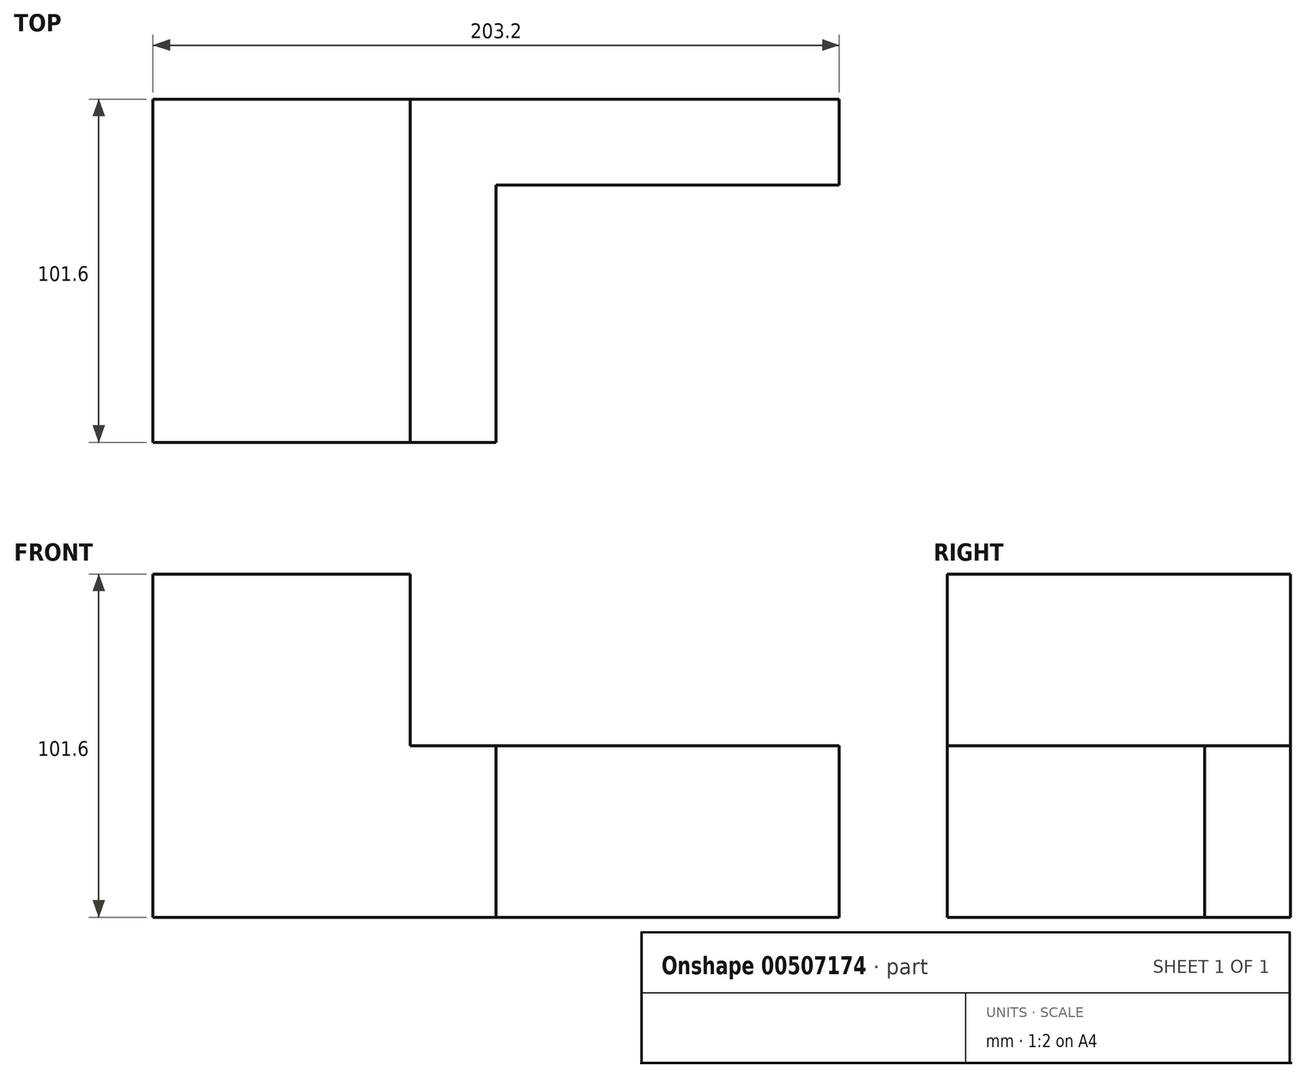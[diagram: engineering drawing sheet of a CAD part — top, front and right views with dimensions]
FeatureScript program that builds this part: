
annotation { "Feature Type Name" : "Feature", "Feature Type Description" : "" }
export const myFeature = defineFeature(function(context is Context, id is Id, definition is map)
    precondition{}
    {
        {
            var Q0;
            Q0=qCreatedBy(makeId("Front.planeOp"),FACE);
            var sketch = newSketch(context, id + "F0", { "sketchPlane" : qUnion([Q0])});
            skLineSegment(sketch, "E0", {"start": v(-76.2, 37.75) * mm, "end": v(0, 37.75) * mm});
            skLineSegment(sketch, "E1", {"start": v(0, 37.75) * mm, "end": v(0, -13.05) * mm});
            skLineSegment(sketch, "E2", {"start": v(0, -13.05) * mm, "end": v(127, -13.05) * mm});
            skLineSegment(sketch, "E3", {"start": v(127, -13.05) * mm, "end": v(127, -63.85) * mm});
            skLineSegment(sketch, "E4", {"start": v(127, -63.85) * mm, "end": v(-76.2, -63.85) * mm});
            skLineSegment(sketch, "E5", {"start": v(-76.2, -63.85) * mm, "end": v(-76.2, 37.75) * mm});
            skSolve(sketch);
        }
        {
            var Q0;
            Q0=qSketchRegion(id+"F0",true);
            extrude(context, id + "F1", {"entities" : qUnion([Q0]), "depth" : 101.6 * mm});
        }
        {
            var Q0;
            Q0=qCreatedBy(makeId("Top.planeOp"),FACE);
            var sketch = newSketch(context, id + "F2", { "sketchPlane" : qUnion([Q0])});
            skLineSegment(sketch, "E6.bottom", {"start": v(127, -101.6) * mm, "end": v(25.4, -101.6) * mm});
            skLineSegment(sketch, "E6.top", {"start": v(127, -25.4) * mm, "end": v(25.4, -25.4) * mm});
            skLineSegment(sketch, "E6.left", {"start": v(127, -101.6) * mm, "end": v(127, -25.4) * mm});
            skLineSegment(sketch, "E6.right", {"start": v(25.4, -101.6) * mm, "end": v(25.4, -25.4) * mm});
            skSolve(sketch);
        }
        {
            var Q0;
            Q0 = qSketchRegion(id + "F2", true);
            extrude(context, id + "F3", {"entities" : qUnion([Q0]), "operationType" : NewBodyOperationType.REMOVE, "oppositeDirection" : true, "depth" : 76.2 * mm});
        }
    });
